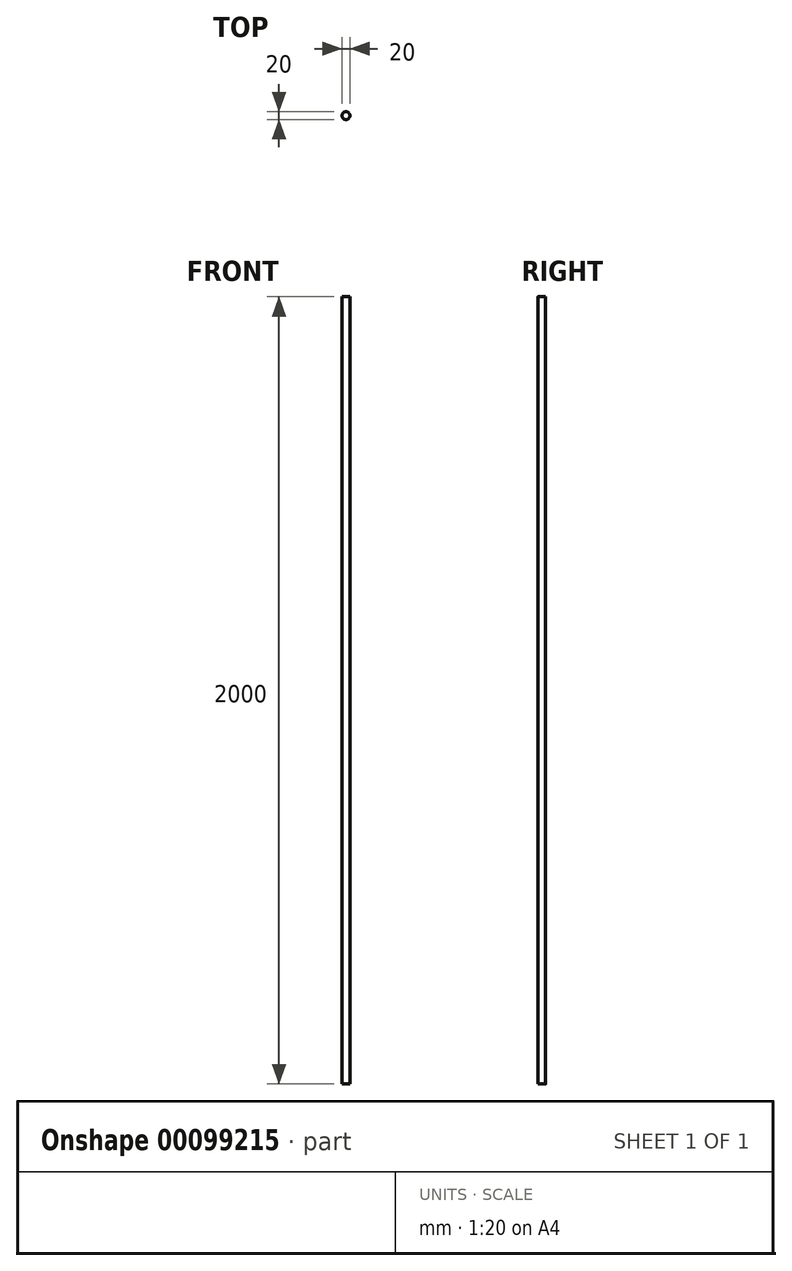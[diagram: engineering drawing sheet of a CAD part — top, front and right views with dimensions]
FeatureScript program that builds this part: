
annotation { "Feature Type Name" : "Feature", "Feature Type Description" : "" }
export const myFeature = defineFeature(function(context is Context, id is Id, definition is map)
    precondition{}
    {
        {
            var Q0;
            Q0=qCreatedBy(makeId("Top.planeOp"),FACE);
            var sketch = newSketch(context, id + "F0", { "sketchPlane" : qUnion([Q0])});
            skCircle(sketch, "E0", {"center": v(-4.8, 0) * mm, "radius": 10 * mm});
            skSolve(sketch);
        }
        {
            var Q0;
            Q0=makeQuery(id+"F0.imprint","IMPRINT",FACE,{"disambiguationData":[TD([[makeQuery(id+"F0.imprint","IMPRINT",EDGE,{"derivedFrom":sQuery(id+"F0.wireOp",EDGE,"E0")}),1.0]])]});
            extrude(context, id + "F1", {"entities" : qUnion([Q0]), "depth" : 2000 * mm});
        }
    });
